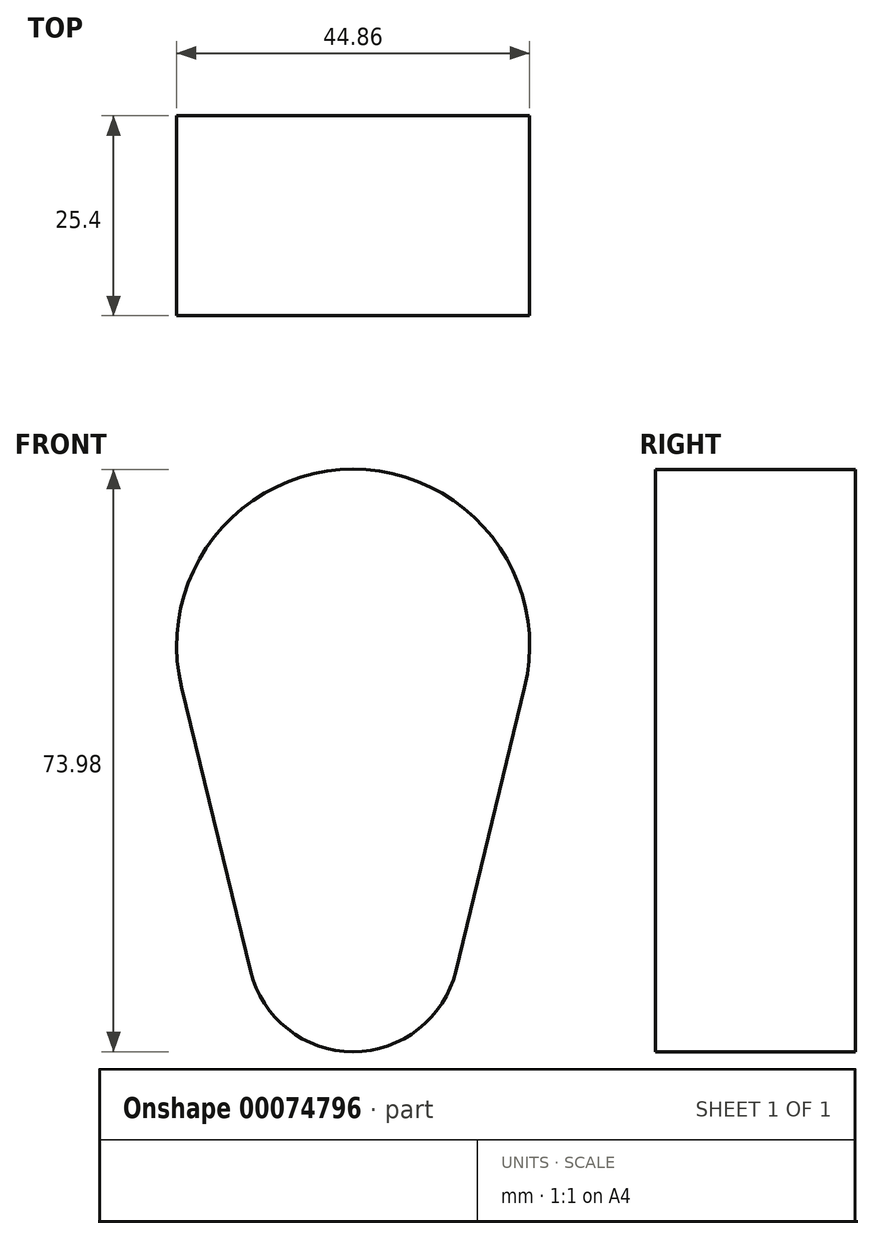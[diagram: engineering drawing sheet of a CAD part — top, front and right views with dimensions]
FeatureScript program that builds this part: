
annotation { "Feature Type Name" : "Feature", "Feature Type Description" : "" }
export const myFeature = defineFeature(function(context is Context, id is Id, definition is map)
    precondition{}
    {
        {
            var Q0;
            Q0=qCreatedBy(makeId("Front.planeOp"),FACE);
            var sketch = newSketch(context, id + "F0", { "sketchPlane" : qUnion([Q0])});
            skArc(sketch, "E0", {"start": v(21.8, 12.95) * mm, "mid": v(0, 40.67) * mm, "end": v(-21.8, 12.95) * mm});
            skArc(sketch, "E1", {"start": v(-13.05, -23.06) * mm, "mid": v(0, -33.31) * mm, "end": v(13.05, -23.06) * mm});
            skLineSegment(sketch, "E2", {"start": v(-21.8, 12.95) * mm, "end": v(-13.05, -23.06) * mm});
            skLineSegment(sketch, "E3", {"start": v(21.8, 12.95) * mm, "end": v(13.05, -23.06) * mm});
            skLineSegment(sketch, "E4", {"start": v(0, 23.04) * mm, "end": v(0, -16.96) * mm});
            skSolve(sketch);
        }
        {
            var Q0;
            Q0 = qSketchRegion(id + "F0", true);
            extrude(context, id + "F1", {"entities" : qUnion([Q0]), "depth" : 25.4 * mm});
        }
    });
